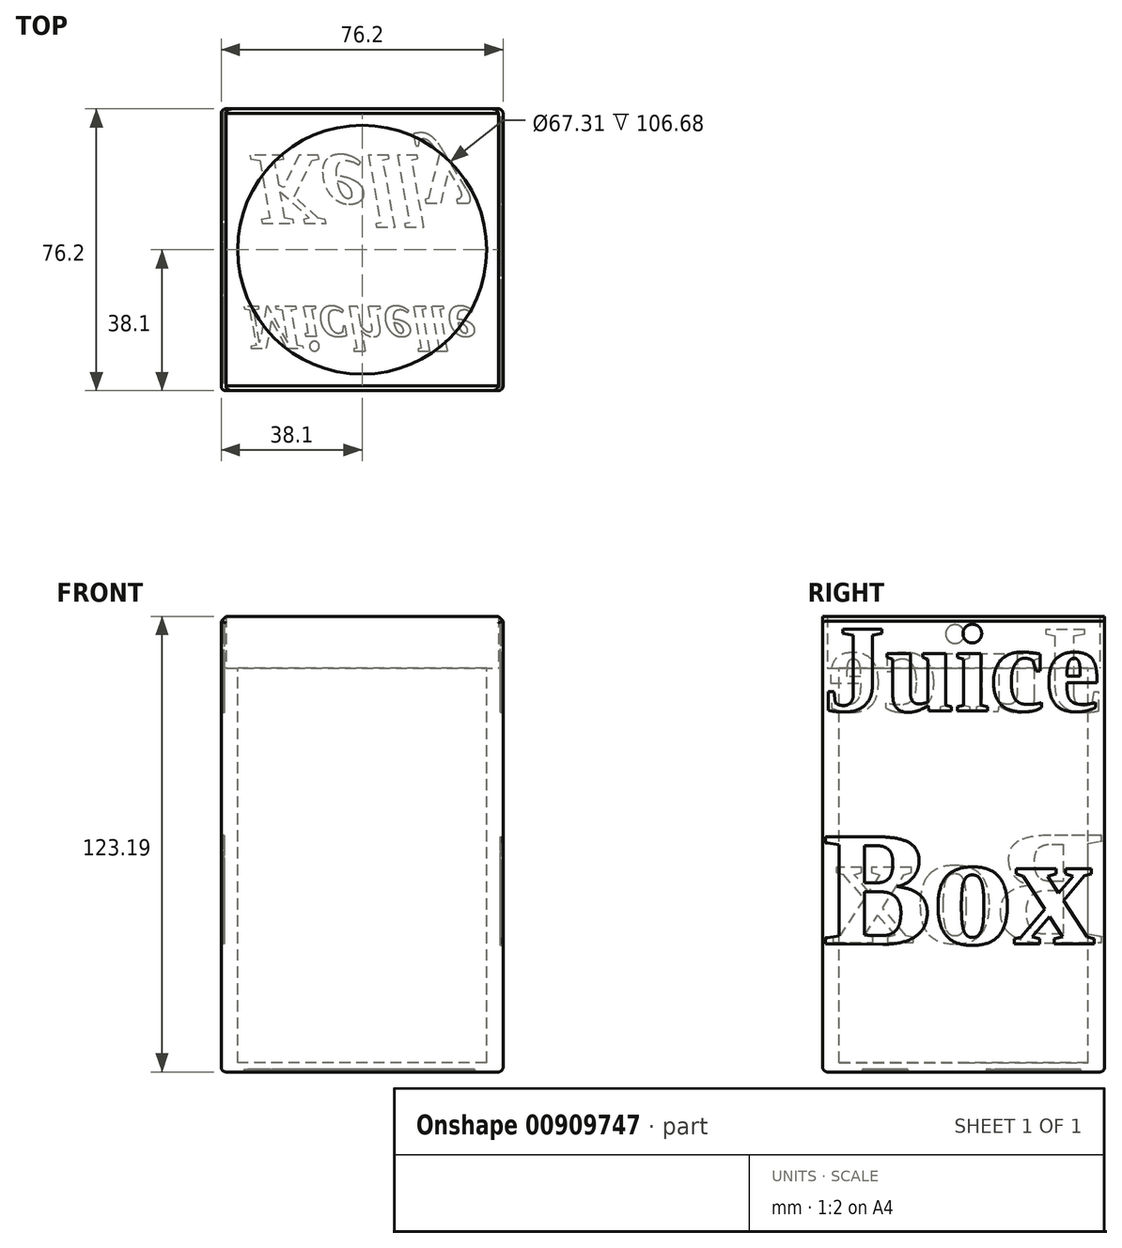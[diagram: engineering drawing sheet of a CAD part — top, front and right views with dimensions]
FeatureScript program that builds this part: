
annotation { "Feature Type Name" : "Feature", "Feature Type Description" : "" }
export const myFeature = defineFeature(function(context is Context, id is Id, definition is map)
    precondition{}
    {
        {
            var Q0;
            Q0=qCreatedBy(makeId("Top.planeOp"),FACE);
            var sketch = newSketch(context, id + "F0", { "sketchPlane" : qUnion([Q0])});
            skLineSegment(sketch, "E0.bottom", {"start": v(-38.1, 38.1) * mm, "end": v(38.1, 38.1) * mm});
            skLineSegment(sketch, "E0.top", {"start": v(-38.1, -38.1) * mm, "end": v(38.1, -38.1) * mm});
            skLineSegment(sketch, "E0.left", {"start": v(-38.1, 38.1) * mm, "end": v(-38.1, -38.1) * mm});
            skLineSegment(sketch, "E0.right", {"start": v(38.1, 38.1) * mm, "end": v(38.1, -38.1) * mm});
            skPoint(sketch, "E0.middle", {"position": v(0, 0) * mm});
            skSolve(sketch);
        }
        {
            var Q0;
            Q0=makeQuery(id+"F0.imprint","IMPRINT",FACE,{"disambiguationData":[TD([[makeQuery(id+"F0.imprint","IMPRINT",EDGE,{"derivedFrom":sQuery(id+"F0.wireOp",EDGE,"E0.bottom")}),-1.0]])]});
            extrude(context, id + "F1", {"entities" : qUnion([Q0]), "endBound" : BoundingType.SYMMETRIC, "depth" : 109.22 * mm, "offsetDistance" : 25.4 * mm});
        }
        {
            var Q0;
            Q0=makeQuery(id+"F1.opExtrude","CAP_FACE",FACE,{"disambiguationData":[OSD([sQuery(id+"F0.wireOp",EDGE,"E0.bottom"),sQuery(id+"F0.wireOp",EDGE,"E0.top"),sQuery(id+"F0.wireOp",EDGE,"E0.left"),sQuery(id+"F0.wireOp",EDGE,"E0.right")])],"isStart":false});
            var sketch = newSketch(context, id + "F2", { "sketchPlane" : qUnion([Q0])});
            skCircle(sketch, "E1", {"center": v(0, 0) * mm, "radius": 33.66 * mm});
            skSolve(sketch);
        }
        {
            var Q0;
            Q0=makeQuery(id+"F2.imprint","IMPRINT",FACE,{"disambiguationData":[TD([[makeQuery(id+"F2.imprint","IMPRINT",EDGE,{"derivedFrom":sQuery(id+"F2.wireOp",EDGE,"E1")}),1.0]])]});
            extrude(context, id + "F3", {"entities" : qUnion([Q0]), "operationType" : NewBodyOperationType.REMOVE, "oppositeDirection" : true, "depth" : 106.68 * mm, "offsetDistance" : 25.4 * mm});
        }
        {
            var Q0;
            Q0=makeQuery(id+"F1.opExtrude","CAP_FACE",FACE,{"disambiguationData":[OSD([sQuery(id+"F0.wireOp",EDGE,"E0.bottom"),sQuery(id+"F0.wireOp",EDGE,"E0.top"),sQuery(id+"F0.wireOp",EDGE,"E0.left"),sQuery(id+"F0.wireOp",EDGE,"E0.right")])],"isStart":false});
            var sketch = newSketch(context, id + "F4", { "sketchPlane" : qUnion([Q0])});
            skLineSegment(sketch, "E2.bottom", {"start": v(-36.83, -36.83) * mm, "end": v(36.83, -36.83) * mm});
            skLineSegment(sketch, "E2.top", {"start": v(-36.83, 36.83) * mm, "end": v(36.83, 36.83) * mm});
            skLineSegment(sketch, "E2.left", {"start": v(-36.83, -36.83) * mm, "end": v(-36.83, 36.83) * mm});
            skLineSegment(sketch, "E2.right", {"start": v(36.83, -36.83) * mm, "end": v(36.83, 36.83) * mm});
            skPoint(sketch, "E2.middle", {"position": v(0, 0) * mm});
            skSolve(sketch);
        }
        {
            var Q0;
            Q0=makeQuery(id+"F4.imprint","IMPRINT",FACE,{"disambiguationData":[TD([[makeQuery(id+"F4.imprint","IMPRINT",EDGE,{"derivedFrom":sQuery(id+"F4.wireOp",EDGE,"E2.bottom")}),-1.0]])]});
            extrude(context, id + "F5", {"entities" : qUnion([Q0]), "operationType" : NewBodyOperationType.ADD, "depth" : 13.97 * mm, "offsetDistance" : 25.4 * mm});
        }
        {
            var Q0;
            Q0=makeQuery(id+"F5.opExtrude","CAP_EDGE",EDGE,{"disambiguationData":[OSD([sQuery(id+"F0.wireOp",EDGE,"E0.left")])],"isStart":false});
            var Q1;
            Q1=makeQuery(id+"F5.opExtrude","CAP_EDGE",EDGE,{"disambiguationData":[OSD([sQuery(id+"F0.wireOp",EDGE,"E0.right")])],"isStart":false});
            chamfer(context, id + "F6", {"entities" : qUnion([Q0, Q1]), "width" : 1.27 * mm, "tangentPropagation" : true});
        }
        {
            var Q0;
            {var subQ0=sQuery(id+"F0.wireOp",EDGE,"E0.left");Q0=makeQuery(id+"F5.boolean.opBoolean","MERGE",FACE,{"derivedFrom":[makeQuery(id+"F1.opExtrude","SWEPT_FACE",FACE,{"disambiguationData":[OSD([subQ0])]}),makeQuery(id+"F5.opExtrude","SWEPT_FACE",FACE,{"disambiguationData":[OSD([subQ0])]})]});}
            var sketch = newSketch(context, id + "F7", { "sketchPlane" : qUnion([Q0])});
            skText(sketch, "E3", { "text": "Juice", "fontName": "Tinos-Bold.ttf"});
            skText(sketch, "E4", { "text": "Box", "fontName": "Tinos-Bold.ttf"});
            const initialGuessF7  = {"E3": [-0.0381, 0.0429, 1, 0, 0.0243], "E4": [-0.0381, -0.0196, 1, 0, 0.03182]};
            skSetInitialGuess(sketch, initialGuessF7);
            skSolve(sketch);
        }
        {
            var Q0;
            {var subQ0=sQuery(id+"F0.wireOp",EDGE,"E0.right");Q0=makeQuery(id+"F5.boolean.opBoolean","MERGE",FACE,{"derivedFrom":[makeQuery(id+"F1.opExtrude","SWEPT_FACE",FACE,{"disambiguationData":[OSD([subQ0])]}),makeQuery(id+"F5.opExtrude","SWEPT_FACE",FACE,{"disambiguationData":[OSD([subQ0])]})]});}
            var sketch = newSketch(context, id + "F8", { "sketchPlane" : qUnion([Q0])});
            skText(sketch, "E5", { "text": "Juice", "fontName": "Tinos-Bold.ttf"});
            skText(sketch, "E6", { "text": "Box", "fontName": "Tinos-Bold.ttf"});
            const initialGuessF8  = {"E5": [-0.0381, 0.04302, 1, 0, 0.0243], "E6": [-0.0381, -0.01998, 1, 0, 0.03182]};
            skSetInitialGuess(sketch, initialGuessF8);
            skSolve(sketch);
        }
        {
            var Q0;
            Q0 = qSketchRegion(id + "F7", true);
            extrude(context, id + "F9", {"entities" : qUnion([Q0]), "operationType" : NewBodyOperationType.REMOVE, "oppositeDirection" : true, "depth" : 0.76 * mm, "offsetDistance" : 25.4 * mm});
        }
        {
            var Q0;
            Q0 = qSketchRegion(id + "F8", true);
            extrude(context, id + "F10", {"entities" : qUnion([Q0]), "operationType" : NewBodyOperationType.REMOVE, "oppositeDirection" : true, "depth" : 0.76 * mm, "offsetDistance" : 25.4 * mm});
        }
        {
            var Q0;
            Q0=makeQuery(id+"F1.opExtrude","CAP_FACE",FACE,{"disambiguationData":[OSD([sQuery(id+"F0.wireOp",EDGE,"E0.bottom"),sQuery(id+"F0.wireOp",EDGE,"E0.top"),sQuery(id+"F0.wireOp",EDGE,"E0.left"),sQuery(id+"F0.wireOp",EDGE,"E0.right")])],"isStart":true});
            var sketch = newSketch(context, id + "F11", { "sketchPlane" : qUnion([Q0])});
            skText(sketch, "E7", { "text": "Michelle", "fontName": "Tinos-BoldItalic.ttf"});
            skText(sketch, "E8", { "text": "Kelly", "fontName": "Tinos-BoldItalic.ttf"});
            const initialGuessF11  = {"E7": [-0.03175, 0.01534, 1, 0, 0.01248], "E8": [-0.03008, -0.02556, 1, 0, 0.02022]};
            skSetInitialGuess(sketch, initialGuessF11);
            skSolve(sketch);
        }
        {
            var Q0;
            Q0 = qSketchRegion(id + "F11", true);
            extrude(context, id + "F12", {"entities" : qUnion([Q0]), "operationType" : NewBodyOperationType.REMOVE, "oppositeDirection" : true, "depth" : 0.76 * mm, "offsetDistance" : 25.4 * mm});
        }
        {
            var Q0;
            {var subQ0=sQuery(id+"F0.wireOp",EDGE,"E0.bottom");Q0=makeQuery(id+"F6.opChamfer","BLEND_EDGE",EDGE,{"blendedFrom":[makeQuery(id+"F5.opExtrude","CAP_EDGE",EDGE,{"disambiguationData":[OSD([sQuery(id+"F0.wireOp",EDGE,"E0.right")])],"isStart":false}),makeQuery(id+"F5.boolean.opBoolean","MERGE",FACE,{"derivedFrom":[makeQuery(id+"F1.opExtrude","SWEPT_FACE",FACE,{"disambiguationData":[OSD([subQ0])]}),makeQuery(id+"F5.opExtrude","SWEPT_FACE",FACE,{"disambiguationData":[OSD([subQ0])]})]})],"blendedInto":[makeQuery(id+"F5.boolean.opBoolean","MERGE",FACE,{"derivedFrom":[makeQuery(id+"F1.opExtrude","SWEPT_FACE",FACE,{"disambiguationData":[OSD([subQ0])]}),makeQuery(id+"F5.opExtrude","SWEPT_FACE",FACE,{"disambiguationData":[OSD([subQ0])]})]})]});}
            var Q1;
            {var subQ0=sQuery(id+"F0.wireOp",EDGE,"E0.right");var subQ1=sQuery(id+"F0.wireOp",EDGE,"E0.bottom");Q1=makeQuery(id+"F5.boolean.opBoolean","MERGE",EDGE,{"derivedFrom":[makeQuery(id+"F1.opExtrude","SWEPT_EDGE",EDGE,{"disambiguationData":[OSD([subQ1,subQ0])]}),makeQuery(id+"F5.opExtrude","SWEPT_EDGE",EDGE,{"disambiguationData":[OSD([subQ1,subQ0])]})]});}
            var Q2;
            {var subQ0=sQuery(id+"F0.wireOp",EDGE,"E0.bottom");Q2=makeQuery(id+"F6.opChamfer","BLEND_EDGE",EDGE,{"blendedFrom":[makeQuery(id+"F5.opExtrude","CAP_EDGE",EDGE,{"disambiguationData":[OSD([sQuery(id+"F0.wireOp",EDGE,"E0.left")])],"isStart":false}),makeQuery(id+"F5.boolean.opBoolean","MERGE",FACE,{"derivedFrom":[makeQuery(id+"F1.opExtrude","SWEPT_FACE",FACE,{"disambiguationData":[OSD([subQ0])]}),makeQuery(id+"F5.opExtrude","SWEPT_FACE",FACE,{"disambiguationData":[OSD([subQ0])]})]})],"blendedInto":[makeQuery(id+"F5.boolean.opBoolean","MERGE",FACE,{"derivedFrom":[makeQuery(id+"F1.opExtrude","SWEPT_FACE",FACE,{"disambiguationData":[OSD([subQ0])]}),makeQuery(id+"F5.opExtrude","SWEPT_FACE",FACE,{"disambiguationData":[OSD([subQ0])]})]})]});}
            var Q3;
            {var subQ0=sQuery(id+"F0.wireOp",EDGE,"E0.left");var subQ1=sQuery(id+"F0.wireOp",EDGE,"E0.bottom");Q3=makeQuery(id+"F5.boolean.opBoolean","MERGE",EDGE,{"derivedFrom":[makeQuery(id+"F1.opExtrude","SWEPT_EDGE",EDGE,{"disambiguationData":[OSD([subQ1,subQ0])]}),makeQuery(id+"F5.opExtrude","SWEPT_EDGE",EDGE,{"disambiguationData":[OSD([subQ1,subQ0])]})]});}
            var Q4;
            {var subQ0=sQuery(id+"F0.wireOp",EDGE,"E0.top");Q4=makeQuery(id+"F6.opChamfer","BLEND_EDGE",EDGE,{"blendedFrom":[makeQuery(id+"F5.opExtrude","CAP_EDGE",EDGE,{"disambiguationData":[OSD([sQuery(id+"F0.wireOp",EDGE,"E0.left")])],"isStart":false}),makeQuery(id+"F5.boolean.opBoolean","MERGE",FACE,{"derivedFrom":[makeQuery(id+"F1.opExtrude","SWEPT_FACE",FACE,{"disambiguationData":[OSD([subQ0])]}),makeQuery(id+"F5.opExtrude","SWEPT_FACE",FACE,{"disambiguationData":[OSD([subQ0])]})]})],"blendedInto":[makeQuery(id+"F5.boolean.opBoolean","MERGE",FACE,{"derivedFrom":[makeQuery(id+"F1.opExtrude","SWEPT_FACE",FACE,{"disambiguationData":[OSD([subQ0])]}),makeQuery(id+"F5.opExtrude","SWEPT_FACE",FACE,{"disambiguationData":[OSD([subQ0])]})]})]});}
            var Q5;
            {var subQ0=sQuery(id+"F0.wireOp",EDGE,"E0.left");var subQ1=sQuery(id+"F0.wireOp",EDGE,"E0.top");Q5=makeQuery(id+"F5.boolean.opBoolean","MERGE",EDGE,{"derivedFrom":[makeQuery(id+"F1.opExtrude","SWEPT_EDGE",EDGE,{"disambiguationData":[OSD([subQ1,subQ0])]}),makeQuery(id+"F5.opExtrude","SWEPT_EDGE",EDGE,{"disambiguationData":[OSD([subQ1,subQ0])]})]});}
            var Q6;
            {var subQ0=sQuery(id+"F0.wireOp",EDGE,"E0.top");Q6=makeQuery(id+"F6.opChamfer","BLEND_EDGE",EDGE,{"blendedFrom":[makeQuery(id+"F5.opExtrude","CAP_EDGE",EDGE,{"disambiguationData":[OSD([sQuery(id+"F0.wireOp",EDGE,"E0.right")])],"isStart":false}),makeQuery(id+"F5.boolean.opBoolean","MERGE",FACE,{"derivedFrom":[makeQuery(id+"F1.opExtrude","SWEPT_FACE",FACE,{"disambiguationData":[OSD([subQ0])]}),makeQuery(id+"F5.opExtrude","SWEPT_FACE",FACE,{"disambiguationData":[OSD([subQ0])]})]})],"blendedInto":[makeQuery(id+"F5.boolean.opBoolean","MERGE",FACE,{"derivedFrom":[makeQuery(id+"F1.opExtrude","SWEPT_FACE",FACE,{"disambiguationData":[OSD([subQ0])]}),makeQuery(id+"F5.opExtrude","SWEPT_FACE",FACE,{"disambiguationData":[OSD([subQ0])]})]})]});}
            var Q7;
            {var subQ0=sQuery(id+"F0.wireOp",EDGE,"E0.right");var subQ1=sQuery(id+"F0.wireOp",EDGE,"E0.top");Q7=makeQuery(id+"F5.boolean.opBoolean","MERGE",EDGE,{"derivedFrom":[makeQuery(id+"F1.opExtrude","SWEPT_EDGE",EDGE,{"disambiguationData":[OSD([subQ1,subQ0])]}),makeQuery(id+"F5.opExtrude","SWEPT_EDGE",EDGE,{"disambiguationData":[OSD([subQ1,subQ0])]})]});}
            var Q8;
            Q8=makeQuery(id+"F1.opExtrude","CAP_EDGE",EDGE,{"disambiguationData":[OSD([sQuery(id+"F0.wireOp",EDGE,"E0.top")])],"isStart":true});
            var Q9;
            Q9=makeQuery(id+"F1.opExtrude","CAP_EDGE",EDGE,{"disambiguationData":[OSD([sQuery(id+"F0.wireOp",EDGE,"E0.left")])],"isStart":true});
            var Q10;
            Q10=makeQuery(id+"F1.opExtrude","CAP_EDGE",EDGE,{"disambiguationData":[OSD([sQuery(id+"F0.wireOp",EDGE,"E0.right")])],"isStart":true});
            var Q11;
            Q11=makeQuery(id+"F1.opExtrude","CAP_EDGE",EDGE,{"disambiguationData":[OSD([sQuery(id+"F0.wireOp",EDGE,"E0.bottom")])],"isStart":true});
            fillet(context, id + "F13", {"entities" : qUnion([Q0, Q1, Q2, Q3, Q4, Q5, Q6, Q7, Q8, Q9, Q10, Q11]), "radius" : 1.27 * mm, "tangentPropagation" : true, "allowEdgeOverflow" : false});
        }
    });
